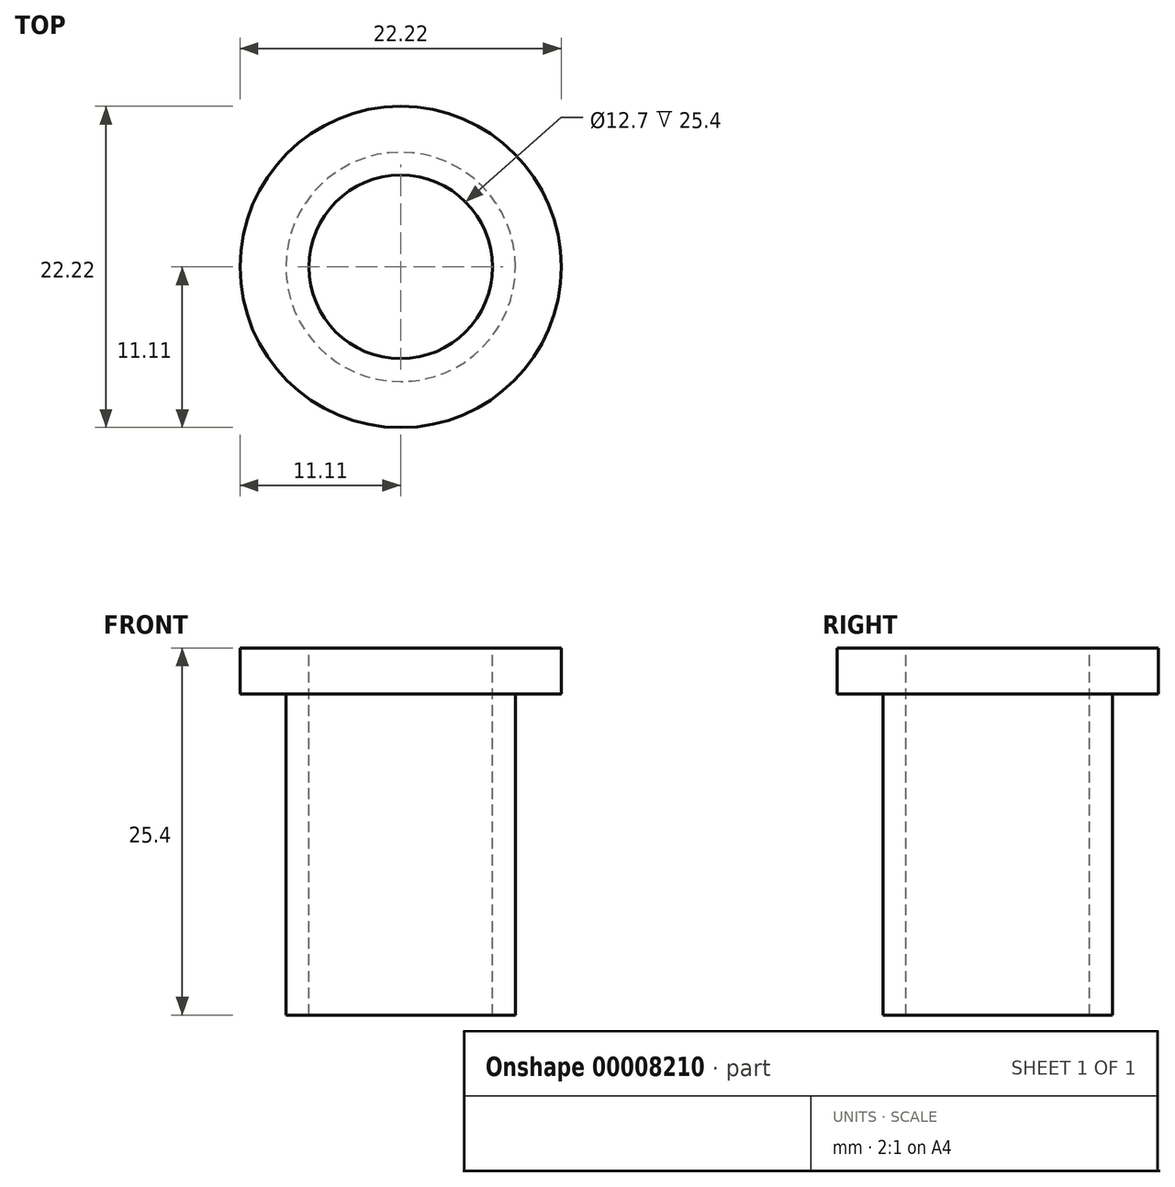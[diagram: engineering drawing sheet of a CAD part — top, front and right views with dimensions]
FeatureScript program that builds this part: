
annotation { "Feature Type Name" : "Feature", "Feature Type Description" : "" }
export const myFeature = defineFeature(function(context is Context, id is Id, definition is map)
    precondition{}
    {
        {
            var Q0;
            Q0=qCreatedBy(makeId("Top.planeOp"),FACE);
            var sketch = newSketch(context, id + "F0", { "sketchPlane" : qUnion([Q0])});
            skCircle(sketch, "E0", {"center": v(0, 0) * mm, "radius": 11.11 * mm});
            skCircle(sketch, "E1", {"center": v(0, 0) * mm, "radius": 6.35 * mm});
            skSolve(sketch);
        }
        {
            var Q0;
            Q0 = qSketchRegion(id + "F0", true);
            extrude(context, id + "F1", {"entities" : qUnion([Q0]), "oppositeDirection" : true, "depth" : 25.4 * mm});
        }
        {
            var Q0;
            Q0=makeQuery(id+"F1.opExtrude","CAP_FACE",FACE,{"disambiguationData":[OSD([sQuery(id+"F0.wireOp",EDGE,"E0"),sQuery(id+"F0.wireOp",EDGE,"E1")])],"isStart":false});
            var sketch = newSketch(context, id + "F2", { "sketchPlane" : qUnion([Q0])});
            skCircle(sketch, "E2", {"center": v(0, 0) * mm, "radius": 7.94 * mm});
            skCircle(sketch, "E3", {"center": v(0, 0) * mm, "radius": 11.11 * mm});
            skSolve(sketch);
        }
        {
            var Q0;
            Q0 = qSketchRegion(id + "F2", true);
            extrude(context, id + "F3", {"entities" : qUnion([Q0]), "operationType" : NewBodyOperationType.REMOVE, "oppositeDirection" : true, "depth" : 22.22 * mm});
        }
    });
